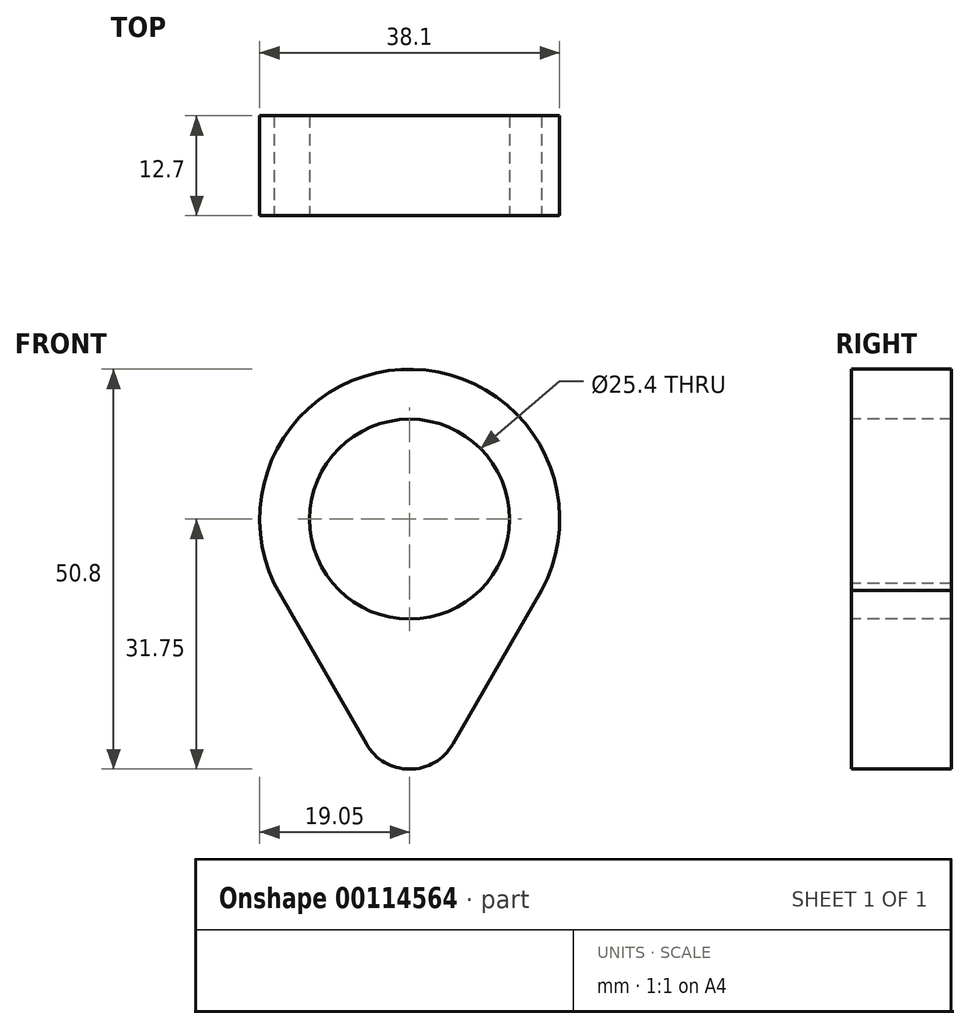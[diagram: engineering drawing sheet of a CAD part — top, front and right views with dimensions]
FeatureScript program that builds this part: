
annotation { "Feature Type Name" : "Feature", "Feature Type Description" : "" }
export const myFeature = defineFeature(function(context is Context, id is Id, definition is map)
    precondition{}
    {
        {
            var Q0;
            Q0=qCreatedBy(makeId("Front.planeOp"),FACE);
            var sketch = newSketch(context, id + "F0", { "sketchPlane" : qUnion([Q0])});
            skCircle(sketch, "E0", {"center": v(0, 0) * mm, "radius": 12.7 * mm});
            skArc(sketch, "E1", {"start": v(16.23, -9.98) * mm, "mid": v(-0.46, 19.04) * mm, "end": v(-15.73, -10.75) * mm});
            skLineSegment(sketch, "E2", {"start": v(0, 0) * mm, "end": v(0, -25.4) * mm});
            skArc(sketch, "E3", {"start": v(-5.5, -28.56) * mm, "mid": v(0, -31.75) * mm, "end": v(5.5, -28.57) * mm});
            skLineSegment(sketch, "E4", {"start": v(-17.22, -8.16) * mm, "end": v(-5.5, -28.56) * mm});
            skLineSegment(sketch, "E5", {"start": v(16.76, -9.05) * mm, "end": v(5.5, -28.57) * mm});
            skSolve(sketch);
        }
        {
            var Q0;
            Q0=makeQuery(id+"F0.imprint","IMPRINT",FACE,{"disambiguationData":[TD([[makeQuery(id+"F0.imprint","IMPRINT",EDGE,{"derivedFrom":sQuery(id+"F0.wireOp",EDGE,"E0")}),-1.0]])]});
            extrude(context, id + "F1", {"entities" : qUnion([Q0]), "oppositeDirection" : true, "depth" : 12.7 * mm});
        }
    });
